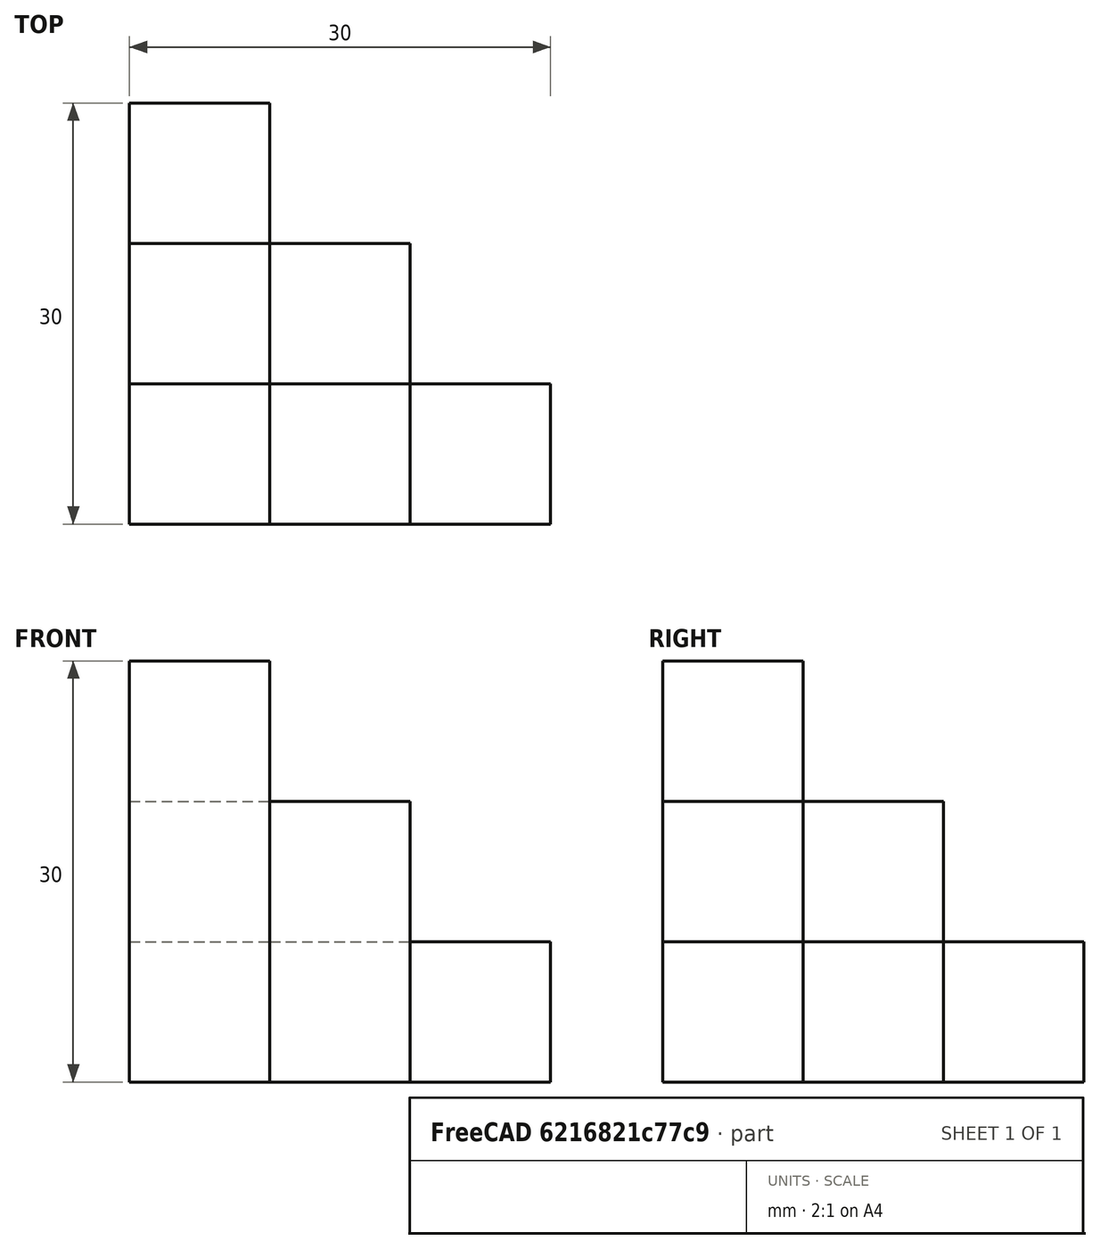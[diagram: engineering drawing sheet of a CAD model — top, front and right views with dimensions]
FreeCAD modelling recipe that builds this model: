
FCSTD DOCUMENT  (FreeCAD 0.18.4R)
Label: tutorial_freecad_ex04
License: All rights reserved
LicenseURL: http://en.wikipedia.org/wiki/All_rights_reserved
objects: Part::Box×6
note: 6 computed .brp shape members not serialized (recipe doc carries the construction recipe); baked Part::Feature solids carry a one-line shape summary decoded from their .brp

FEATURE [Part::Box] Box  label="Nivel01_cubo01"
  AttacherType = Attacher::AttachEngine3D
  Height = 30
  Length = 10
  Width = 10
FEATURE [Part::Box] Box001  label="Nivel02_cubo01"
  AttacherType = Attacher::AttachEngine3D
  Height = 20
  Length = 10
  Placement = pos=(10,0,0) rot=(0,0,1;0rad)
  Width = 10
FEATURE [Part::Box] Box002  label="Nivel02_cubo02"
  AttacherType = Attacher::AttachEngine3D
  Height = 20
  Length = 10
  Placement = pos=(0,10,0) rot=(0,0,1;0rad)
  Width = 10
FEATURE [Part::Box] Box003  label="Nivel03_cubo001"
  AttacherType = Attacher::AttachEngine3D
  Height = 10
  Length = 10
  Placement = pos=(20,0,0) rot=(0,0,1;0rad)
  Width = 10
FEATURE [Part::Box] Box004  label="Nivel03_cubo002"
  AttacherType = Attacher::AttachEngine3D
  Height = 10
  Length = 10
  Placement = pos=(0,20,0) rot=(0,0,1;0rad)
  Width = 10
FEATURE [Part::Box] Box005  label="Nivel03_cubo003"
  AttacherType = Attacher::AttachEngine3D
  Height = 10
  Length = 10
  Placement = pos=(10,10,0) rot=(0,0,1;0rad)
  Width = 10
